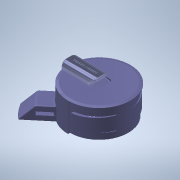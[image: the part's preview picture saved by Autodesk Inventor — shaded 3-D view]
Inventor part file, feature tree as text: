
AUTODESK INVENTOR PART (.ipt)
format: ipt  version: 2020 (Build 240168000, 168)  size: 4,051,968 bytes
history: native  units: mm
features: extrude x51, sketch x22, fillet x22, other x14, plane x9, boolean_combine x7, thread x7, projected_geometry x7, hole x4, revolve x3, shell x3, chamfer x3, move_body x1
ambient origin geometry x8: Origin, YZ Plane, XZ Plane, XY Plane, X Axis, Y Axis, Z Axis, Center Point
bodies: Solid7 (feature_tree), Solid8 (feature_tree), Solid9 (feature_tree), Solid13 (feature_tree)
feature tree (153):
  other  "AroPrincipal"
  extrude  "Extrusion1"  Depth=2.5mm
  sketch  "Sketch3"  dims[d0=90.0mm d1=2.5mm]
  extrude  "Patitas"  Depth=24.43461mm
  revolve  "Revolution1"  [1 undecoded]
  plane  "Work Plane1"
  extrude  "Extrusion3"  Depth=15.0mm
  sketch  "Sketch7"  dims[d7=180.0mm d8=15.0mm]
  revolve  "Revolution2"  [1 undecoded]
  revolve  "Revolution3"  [1 undecoded]
  extrude  "Extrusion4"  Depth=20.0mm
  plane  "Work Plane2"
  extrude  "Extrusion5"  Depth=15.0mm
  extrude  "Extrusion6"  Depth=5.0mm
  plane  "Work Plane3"
  extrude  "Extrusion7"  Depth=7.5mm
  sketch  "Sketch11"  dims[d20=15.0mm d21=15.0mm]
  extrude  "Extrusion10"  TaperAngle=90.0deg  [1 undecoded]
  extrude  "Extrusion11"  Depth=90.0mm
  extrude  "Extrusion17"  Depth=85.0mm
  plane  "Work Plane4"
  move_body  "Move Body2"
  extrude  "Extrusion21"  Depth=16.580628mm
  plane  "Work Plane5"
  extrude  "Extrusion22"  Depth=10.0mm
  plane  "Work Plane6"
  extrude  "Extrusion23"  Depth=20.0mm
  sketch  "Sketch24"  dims[d24=20.0mm d25=7.5mm]
  extrude  "Extrusion24"  Depth=1.0mm
  extrude  "Extrusion25"  Depth=85.0mm
  shell  "Shell1"  Thickness=43.0mm
  shell  "Shell2"  Thickness=96.0mm
  hole  "Hole1"  [1 undecoded]
  hole  "Hole2"  [1 undecoded]
  boolean_combine  "Combine3"
  extrude  "Extrusion26"  Depth=10.0mm TaperAngle=0.0deg
  extrude  "Extrusion27"  Depth=3.0mm
  sketch  "Sketch25"  dims[d26=5.0mm d27=90.0deg]
  extrude  "Extrusion28"  Depth=30.0mm TaperAngle=0.0deg
  plane  "Work Plane7"
  sketch  "Sketch26"  dims[d28=10.0mm d29=90.0mm]
  extrude  "Extrusion30"  Depth=43.0mm
  extrude  "Extrusion31"  Depth=96.0mm
  thread  "Thread2"  [1 undecoded]
  thread  "Thread3"  [1 undecoded]
  thread  "Thread4"  [1 undecoded]
  extrude  "Extrusion32"  Depth=15.0mm
  boolean_combine  "Combine4"
  fillet  "Fillet4"  Radius=11.43mm
  fillet  "Fillet8"  Radius=2.0mm
  fillet  "Fillet9"  Radius=2.0mm
  plane  "Work Plane8"
  sketch  "Sketch30"  dims[d37=20.0mm d38=0.0mm d39=16.580628mm]
  extrude  "Extrusion33"  Depth=4.6mm
  extrude  "Extrusion34"  Depth=2.2mm
  fillet  "fillet hold screw core"  Radius=6.0mm
  extrude  "Extrusion36"  Depth=6.8mm
  fillet  "Fillet11"  Radius=20.0mm
  hole  "Hole3"  [1 undecoded]
  extrude  "Extrusion37"  Depth=25.0mm
  fillet  "Fillet12"  Radius=1.1mm
  plane  "Work Plane9"
  extrude  "Extrusion38"  Depth=12.5mm
  extrude  "Extrusion39"  Depth=8.0mm
  fillet  "Fillet13"  Radius=15.0mm
  fillet  "Fillet14"  Radius=5.0mm
  extrude  "Extrusion40"  Depth=31.4mm
  extrude  "Extrusion41"  Depth=31.4mm
  other  "Battery holder 1"
  extrude  "Battery holder"  Depth=3.5mm
  hole  "Hole4"  [1 undecoded]
  extrude  "Extrusion44"  Depth=14.2mm
  extrude  "Extrusion45"  Depth=31.4mm
  extrude  "Extrusion46"  Depth=16.1mm
  extrude  "Extrusion47"  Depth=6.0mm TaperAngle=0.0deg
  extrude  "Extrusion48"  Depth=96.0mm
  extrude  "Extrusion49"  [1 undecoded]
  extrude  "Extrusion50"  TaperAngle=0.0deg  [1 undecoded]
  extrude  "Extrusion51"  Depth=2.5mm TaperAngle=0.0deg
  extrude  "Extrusion52"  Depth=8.5mm
  fillet  "Fillet15"  Radius=96.0mm
  chamfer  "Chamfer1"  Distance=85.0mm
  sketch  "Sketch36"  dims[d51=10.0mm d52=2.0mm d53=35.0mm d54=4.0mm d55=2.0mm]
  extrude  "Extrusion53"  Depth=96.0mm
  extrude  "Extrusion56"  Depth=35.0mm
  extrude  "Extrusion57"  Depth=1.5mm
  extrude  "Extrusion58"  Depth=2.0mm
  thread  "Thread5"  [1 undecoded]
  thread  "Thread6"  [1 undecoded]
  thread  "Thread7"  [1 undecoded]
  thread  "Thread8"  [1 undecoded]
  chamfer  "Chamfer2"  Distance=3.0mm
  fillet  "Fillet17"  Radius=85.0mm
  other  "tapa PPG"
  other  "tapa up PPG"
  extrude  "Extrusion61"  Depth=85.0mm
  sketch  "Sketch41"  dims[d56=3.0mm d57=96.0mm]
  extrude  "Extrusion66"  Depth=35.0mm
  fillet  "Fillet19"  Radius=15.0mm
  boolean_combine  "Combine5"
  boolean_combine  "Combine6"
  shell  "Shell4"  Thickness=30.0mm
  extrude  "Extrusion67"  Depth=1.5mm
  other  "plano sup sup"
  extrude  "Extrusion68"  Depth=14.0mm TaperAngle=0.0deg
  extrude  "Extrusion69"  Depth=7.0mm
  fillet  "Fillet22"  Radius=7.0mm
  fillet  "Fillet23"  Radius=7.0mm
  fillet  "Fillet24"  Radius=7.0mm
  boolean_combine  "Combine7"
  fillet  "Fillet25"  Radius=12.0mm
  extrude  "Extrusion70"  Depth=12.0mm
  boolean_combine  "Combine8"
  extrude  "Extrusion71"  Depth=10.0mm TaperAngle=0.0deg
  fillet  "Fillet26"  Radius=12.0mm
  fillet  "Fillet28"  Radius=2.0mm
  fillet  "Fillet29"  Radius=1.5mm
  chamfer  "Chamfer3"  Distance=1.5mm
  boolean_combine  "Combine10"
  fillet  "Fillet30"  Radius=4.0mm
  extrude  "Extrusion72"  Depth=2.0mm
  fillet  "Fillet31"  Radius=4.0mm
  fillet  "Fillet32"  Radius=2.0mm
  fillet  "Fillet33"  Radius=14.0mm
  sketch  "Sketch5"  dims[d2=43.0mm d3=0.0mm d4=24.43461mm]
  sketch  "Sketch6"  dims[d5=90.0mm d6=6.981317mm]
  other  "Enganche"
  sketch  "Sketch8"  dims[d9=15.0mm d11=20.0mm d12=0.0mm]
  sketch  "Sketch9"  dims[d15=20.0mm d16=90.0mm]
  projected_geometry  "Projected Loop1"
  sketch  "Sketch10"  dims[d18=180.0deg d19=20.0mm]
  other  "tapa"
  projected_geometry  "Projected Loop2"
  other  "Fingertip"
  sketch  "Sketch20"  dims[d22=25.0mm d23=5.0mm]
  other  "inf RR"
  other  "reflector"
  projected_geometry  "Projected Loop7"
  projected_geometry  "Projected Loop8"
  projected_geometry  "Projected Loop9"
  sketch  "Sketch28"  dims[d30=96.0mm d36=85.0mm]
  sketch  "Sketch31"  dims[d40=16.580628mm d41=10.0mm]
  other  "tapa RR"
  sketch  "Sketch32"  dims[d42=2.5mm d43=20.0mm]
  sketch  "Sketch33"  dims[d44=29.84513mm d45=1.0mm]
  sketch  "Sketch34"  dims[d46=0.174533mm d47=85.0mm d48=43.0mm d49=0.0mm d50=96.0mm]
  other  "forma dedo"
  other  "PPG cover"
  sketch  "Sketch42"  dims[d58=2.0mm d59=10.0mm d60=0.0mm]
  other  "forma dedo sup"
  sketch  "Sketch44"  dims[d61=35.0mm d62=3.0mm d63=30.0mm d64=0.0mm d65=43.0mm d66=96.0mm d67=2.5mm d68=0.0mm d78=18.54mm d79=14.2mm d80=15.0mm d81=11.43mm d82=2.0mm d83=2.0mm d84=4.6mm d85=2.2mm d86=6.0mm d87=6.8mm d88=20.0mm d90=40.0mm d91=25.0mm d94=1.1mm d95=12.5mm d96=8.0mm d97=15.0mm d98=0.0mm d110=5.0mm d111=0.0mm d122=31.4mm d123=31.4mm d124=3.5mm d125=0.5mm d126=14.2mm d131=31.4mm d132=16.1mm d139=6.0mm d140=0.0mm d144=96.0mm d145=-48.0mm d152=0.0mm d153=-17.5mm d154=0.0mm d163=2.5mm d164=0.0mm d171=8.5mm d172=96.0mm d173=85.0mm d174=96.0mm d175=35.0mm d176=1.5mm d177=2.0mm d178=2.0mm d179=3.0mm d180=30.0mm d181=2.0mm d182=0.0mm d183=3.0mm d184=85.0mm d185=85.0mm d186=35.0mm d188=15.0mm d189=30.0mm d190=1.5mm d191=14.0mm d192=0.0mm d195=7.0mm d196=7.0mm d197=7.0mm d198=7.0mm d199=12.0mm d200=12.0mm d201=10.0mm d202=0.0mm d203=12.0mm d204=0.0mm d205=2.0mm d206=1.5mm d207=1.5mm d208=7.0mm d209=6.0mm d210=4.0mm d211=2.0mm d212=90.0deg d213=8.0mm d214=20.594885mm d215=7.0mm d216=6.0mm d217=4.0mm d218=2.0mm d219=90.0deg d220=8.0mm d221=20.594885mm d222=4.0mm d223=2.0mm d224=4.0mm d225=2.0mm d226=14.0mm d227=0.0mm d228=10.0mm d229=34.0mm d230=10.5mm d231=0.0mm d232=0.5mm d233=10.0mm d234=2.5mm d235=36.1mm d236=0.0mm d239=-42.5mm d242=2.5mm d243=1.5mm d244=3.0mm d245=2.5mm d246=1.5mm d247=3.0mm d249=0.15mm d251=54.0mm d252=0.0mm d254=10.0mm d255=34.0mm d256=3.0mm d257=3.0mm d258=3.0mm d259=5.0mm d260=5.0mm d261=5.0mm d262=5.0mm d263=5.0mm d264=3.5mm d265=0.0mm d268=3.5mm d269=0.0mm d270=3.5mm d271=0.0mm d272=3.5mm d273=0.0mm d274=3.5mm d275=0.0mm d276=10.0mm d280=5.0mm d282=10.5mm d283=1.0mm d284=0.5mm d285=1.0mm d286=0.75mm d287=6.5mm d288=96.0mm d289=85.0mm d290=96.0mm d291=35.0mm d292=1.5mm d293=2.0mm d294=2.0mm d295=3.0mm d296=30.0mm d297=2.0mm d298=0.0mm d299=25.0mm d300=3.0mm d301=0.0mm d302=10.0mm d303=6.0mm d304=10.0mm d307=2.0mm d308=0.0mm d309=1.5mm d310=3.0mm d311=4.5mm d312=5.0mm d313=3.0mm d314=2.5mm d315=3.0mm d316=5.98424mm d317=3.023mm d318=2.0mm d319=14.3117mm d320=2.0mm d321=0.0mm d322=1.5mm d323=1.5mm d324=58.5mm d325=0.0mm d326=1.0mm d327=0.25mm d328=23.9mm d329=85.0mm d332=1.3mm d333=0.0mm d334=10.0mm d335=5.0mm d336=45.0deg d337=0.4mm d338=0.0mm d339=0.25mm d340=0.2mm d346=0.1mm d347=0.1mm d348=0.1mm d349=1.0mm d350=0.75mm d352=0.5mm d353=1.3mm d354=0.0mm d355=0.5mm d356=0.0mm d357=0.5mm d358=85.0mm d359=90.0deg d360=25.0mm d361=96.0mm d362=38.0mm d367=20.0mm d368=0.0mm d369=1.5mm d370=14.67mm d371=0.0mm d372=20.0mm d373=6.0mm d374=4.0mm d375=2.0mm d376=90.0deg d377=12.67mm d378=0.0mm d381=6.17mm d382=0.0mm d383=4.67mm d384=0.0mm d385=4.67mm d386=0.0mm d387=6.5mm d388=13.438mm d389=3.2mm d390=0.5mm d391=0.7mm d392=13.17mm d393=0.0mm d394=13.17mm d395=0.0mm d396=0.5mm d397=3.25mm d406=0.0mm d409=13.0mm d411=10.0mm d412=0.0mm d413=6.5mm d414=1.5mm d415=1.5mm d416=3.5mm d417=6.5mm d418=1.5mm d419=0.5mm d420=0.7mm d421=2.5mm d422=0.0mm d423=2.5mm d424=0.0mm d425=2.5mm d426=0.0mm d427=2.0mm d428=0.5mm d429=5.0mm d430=7.25mm d431=45.0deg d432=8.0mm d433=20.0mm d434=1.25mm d435=85.0mm d436=20.0mm d437=1.25mm d438=2.0mm d439=0.0mm d440=90.0mm d441=180.0mm d442=85.0mm d443=73.0mm d452=6.0mm d458=2.0mm d459=2.0mm d460=96.0mm d461=2.0mm d462=2.0mm d463=4.0mm d464=8.0mm d465=8.0mm d466=4.0mm d467=4.0mm d468=4.0mm d469=4.0mm d470=6.0mm d471=6.0mm d472=3.0mm d473=3.0mm d474=3.0mm d475=3.0mm d476=5.0mm d477=0.0mm d478=2.0mm d479=0.0mm d480=5.0mm d481=0.0mm d482=3.5mm d483=0.0mm d484=3.5mm d485=0.0mm d486=3.5mm d487=0.0mm d488=3.5mm d489=0.0mm d490=5.0mm d491=2.0mm d492=45.0deg d493=5.0mm d504=15.0mm d512=60.0deg d534=4.0mm d535=2.0mm d536=10.0mm d545=10.0mm d548=15.0mm d549=4.363323mm d550=4.0mm d551=2.0mm d552=10.0mm d553=10.0mm d554=15.0mm d555=2.5mm d558=25.0mm d559=0.0mm d576=96.0mm d577=70.0mm d578=20.0mm d579=7.0mm d580=10.5mm d581=0.0mm d582=8.5mm d583=2.0mm d584=25.0mm d585=0.0mm d586=55.5mm d587=96.0mm d588=70.0mm d589=25.0mm d590=10.0mm d591=0.0mm d592=2.0mm d593=0.0mm d596=177.0mm d597=17.75mm d598=11.0mm d599=17.75mm d600=11.0mm d601=10.0mm d602=10.0mm d603=6.0mm d604=10.0mm d605=0.0mm d606=40.0mm d607=14.5mm d608=0.0mm d609=0.0mm d610=8.0mm d611=2.0mm d612=10.0mm d616=1.0mm d617=2.0mm d618=5.0mm d619=0.5mm d620=4.0mm d621=1.0mm d622=45.0deg d623=1.0mm d624=9.0mm d625=2.75mm d626=40.0mm d627=1.5mm d628=0.0mm d629=0.5mm d630=27.0mm d631=4.0mm d632=1.0mm d633=2.0mm d634=1.0mm d635=1.0mm]
  projected_geometry  "Project Cut Edges1"
  projected_geometry  "Project Cut Edges2"
note: 17 required parameter values undecoded (feature->parameter linkage not recoverable at this tier; creation-order binding heuristic only, values carry confidence <= 0.55)